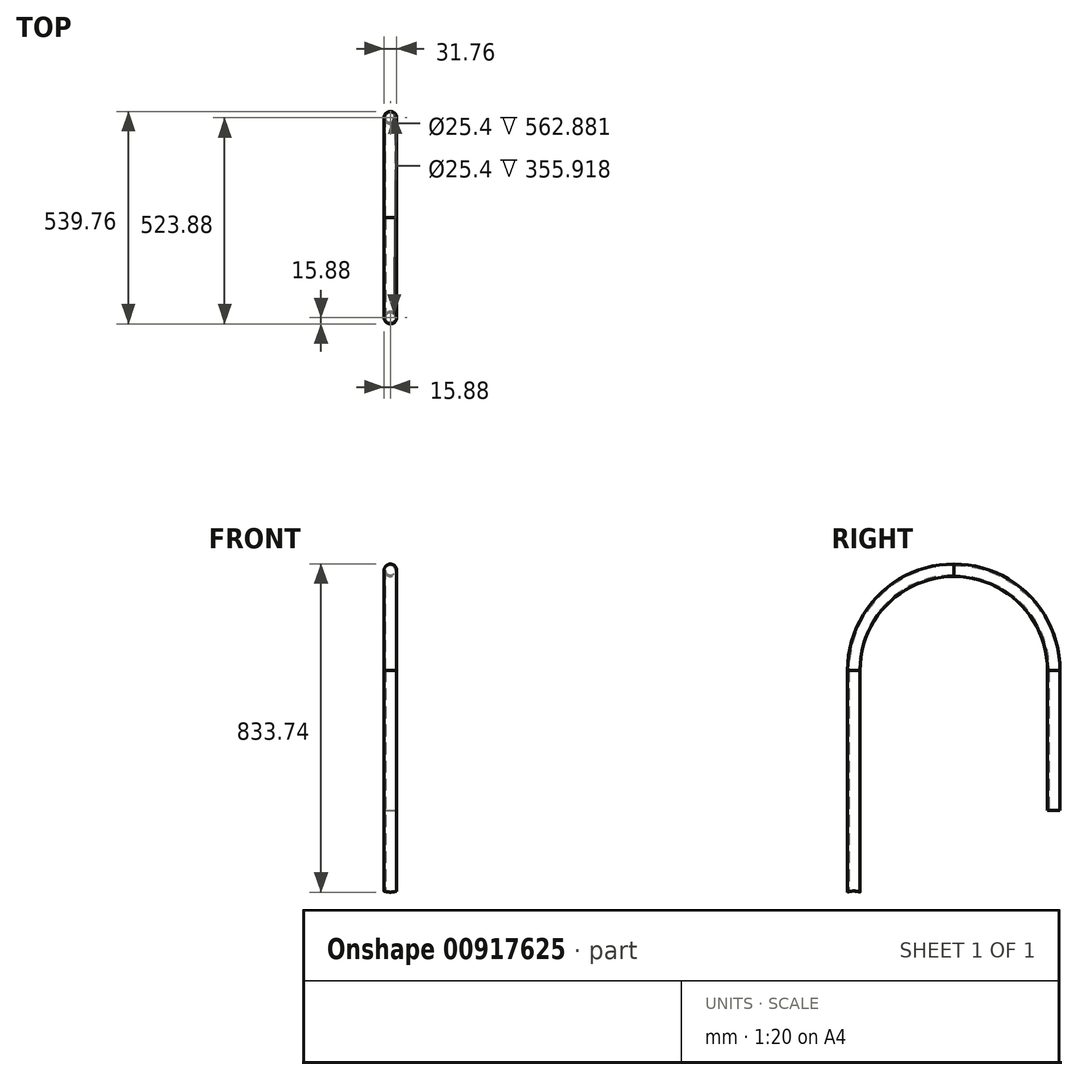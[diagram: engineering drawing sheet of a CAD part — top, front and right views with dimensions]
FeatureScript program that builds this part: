
annotation { "Feature Type Name" : "Feature", "Feature Type Description" : "" }
export const myFeature = defineFeature(function(context is Context, id is Id, definition is map)
    precondition{}
    {
        {
            var Q0;
            Q0=qCreatedBy(makeId("Top.planeOp"),FACE);
            var sketch = newSketch(context, id + "F0", { "sketchPlane" : qUnion([Q0])});
            skCircle(sketch, "E0", {"center": v(0, 0) * mm, "radius": 15.88 * mm});
            skCircle(sketch, "E1", {"center": v(0, 0) * mm, "radius": 12.7 * mm});
            skSolve(sketch);
        }
        {
            var Q0;
            Q0=makeQuery(id+"F0.imprint","IMPRINT",FACE,{"disambiguationData":[TD([[makeQuery(id+"F0.imprint","IMPRINT",EDGE,{"derivedFrom":sQuery(id+"F0.wireOp",EDGE,"E0")}),1.0]])]});
            extrude(context, id + "F1", {"entities" : qUnion([Q0]), "depth" : 609.6 * mm, "offsetDistance" : 25.4 * mm});
        }
        {
            var Q0;
            Q0=qCreatedBy(makeId("Right.planeOp"),FACE);
            var sketch = newSketch(context, id + "F2", { "sketchPlane" : qUnion([Q0])});
            skLineSegment(sketch, "E2.0", {"start": v(-15.88, 609.6) * mm, "end": v(15.88, 609.6) * mm, "construction": true});
            skArc(sketch, "E3", {"start": v(0, 609.6) * mm, "mid": v(-74.4, 789.2) * mm, "end": v(-254, 863.6) * mm});
            skLineSegment(sketch, "E4", {"start": v(0, 126.4) * mm, "end": v(0, 609.6) * mm, "construction": true});
            skSolve(sketch);
        }
        {
            var Q0;
            Q0=makeQuery(id+"F1.opExtrude","CAP_FACE",FACE,{"disambiguationData":[OSD([sQuery(id+"F0.wireOp",EDGE,"E0"),sQuery(id+"F0.wireOp",EDGE,"E1")])],"isStart":false});
            var sketch = newSketch(context, id + "F3", { "sketchPlane" : qUnion([Q0])});
            skCircle(sketch, "E5.0", {"center": v(0, 0) * mm, "radius": 15.88 * mm});
            skLineSegment(sketch, "E6", {"start": v(0, -254) * mm, "end": v(16.73, -254) * mm, "construction": true});
            skCircle(sketch, "E7.0", {"center": v(0, 0) * mm, "radius": 12.7 * mm});
            skSolve(sketch);
        }
        {
            var Q0;
            Q0 = qSketchRegion(id + "F3", true);
            var Q1;
            Q1=sQuery(id+"F2.wireOp",EDGE,"E3");
            sweep(context, id + "F4", {"profiles" : qUnion([Q0]), "path" : qUnion([Q1])});
        }
        {
            var Q0;
            Q0 = qSketchRegion(id + "F3", true);
            var Q1;
            Q1=sQuery(id+"F3.wireOp",EDGE,"E6");
            revolve(context, id + "F5", {"surfaceOperationType" : NewSurfaceOperationType.NEW, "entities" : qUnion([Q0]), "axis" : qUnion([Q1]), "revolveType" : RevolveType.ONE_DIRECTION, "angle" : 90 * degree});
        }
        {
            var Q0;
            Q0=makeQuery(id+"F1.opExtrude","SWEPT_BODY",BODY,{"disambiguationData":[OSD([sQuery(id+"F0.wireOp",EDGE,"E0"),sQuery(id+"F0.wireOp",EDGE,"E1")])]});
            var Q1;
            Q1=makeQuery(id+"F5.opRevolve","SWEPT_BODY",BODY,{"disambiguationData":[OSD([sQuery(id+"F3.wireOp",EDGE,"E5.0"),sQuery(id+"F3.wireOp",EDGE,"E7.0")])]});
            var Q2;
            Q2=makeQuery(id+"F5.opRevolve","CAP_FACE",FACE,{"disambiguationData":[OSD([sQuery(id+"F3.wireOp",EDGE,"E5.0"),sQuery(id+"F3.wireOp",EDGE,"E7.0")])],"isStart":false});
            mirror(context, id + "F6", {"entities" : qUnion([Q0, Q1]), "mirrorPlane" : qUnion([Q2])});
        }
        {
            var Q0;
            Q0=qCreatedBy(makeId("Right.planeOp"),FACE);
            var sketch = newSketch(context, id + "F7", { "sketchPlane" : qUnion([Q0])});
            skCircle(sketch, "E8", {"center": v(0, 0) * mm, "radius": 254 * mm});
            skCircle(sketch, "E9", {"center": v(-508, 0) * mm, "radius": 48.42 * mm});
            skLineSegment(sketch, "E10.0", {"start": v(-492.13, 0) * mm, "end": v(-523.88, 0) * mm, "construction": true});
            skSolve(sketch);
        }
        {
            var Q0;
            Q0 = qSketchRegion(id + "F7", true);
            extrude(context, id + "F8", {"entities" : qUnion([Q0]), "operationType" : NewBodyOperationType.REMOVE, "endBound" : BoundingType.SYMMETRIC, "depth" : 127 * mm, "offsetDistance" : 25.4 * mm});
        }
    });
